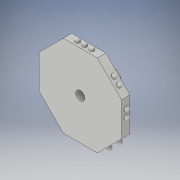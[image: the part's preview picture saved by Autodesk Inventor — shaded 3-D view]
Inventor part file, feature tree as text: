
AUTODESK INVENTOR PART (.ipt)
format: ipt  version: 2017 (Build 210142000, 142)  size: 347,648 bytes
history: native  units: in
note: dims shown in document units (in); Inventor stores cm internally (conversion verified against a paired STEP export)
features: sketch x11, extrude x10, fillet x7, pattern_circular x1
ambient origin geometry x8: Origin, YZ Plane, XZ Plane, XY Plane, X Axis, Y Axis, Z Axis, Center Point
bodies: Solid1 (feature_tree)
feature tree (29):
  extrude  "Extrusion1"  Depth=0.1181in TaperAngle=0.0deg
  extrude  "Extrusion2"  Depth=0.063in
  fillet  "Fillet1"  Radius=0.1in
  sketch  "Sketch3"  dims[d8=0.063in d9=0.063in d10=0.059in]
  sketch  "Sketch4"  dims[d11=0.0472in d12=0.0in d13=0.0315in d24=0.059in]
  sketch  "Sketch5"  dims[d25=0.063in d26=0.1in d27=0.1in d28=0.063in d29=0.063in d31=0.0575in d32=0.059in d34=0.0in d35=0.059in]
  sketch  "Sketch6"  dims[d36=0.059in]
  sketch  "Sketch7"  dims[d40=0.063in d41=0.1in d42=0.1in d43=0.063in d44=0.063in d46=0.059in d47=0.0in d48=0.059in d49=0.059in d50=0.0in d51=0.0in]
  sketch  "Sketch8"  dims[d70=0.063in d71=0.1in d72=0.1in d73=0.063in d74=0.063in d76=0.059in d77=0.0in d78=0.059in d79=0.059in d81=0.0in d82=0.0in]
  sketch  "Sketch9"  dims[d83=0.063in d84=0.1in d85=0.1in d86=0.063in d87=0.063in d89=0.059in d90=0.059in d91=0.059in d92=0.0in d93=0.0in d94=0.0in d95=0.0in]
  extrude  "Extrusion6"  Depth=0.063in
  fillet  "Fillet5"  Radius=0.059in
  extrude  "Extrusion7"  Depth=0.0315in
  fillet  "Fillet6"  Radius=0.059in
  extrude  "Extrusion8"  TaperAngle=0.0deg  [1 undecoded]
  fillet  "Fillet7"  Radius=0.059in
  extrude  "Extrusion9"  TaperAngle=0.0deg  [1 undecoded]
  fillet  "Fillet8"  [1 undecoded]
  extrude  "Extrusion10"  TaperAngle=0.0deg  [1 undecoded]
  fillet  "Fillet9"  [1 undecoded]
  extrude  "Extrusion11"  TaperAngle=0.0deg  [1 undecoded]
  fillet  "Fillet10"  [1 undecoded]
  extrude  "Extrusion14"  Depth=0.0315in
  pattern_circular  "Circular Pattern4"  [2 undecoded]
  extrude  "Extrusion15"  Depth=0.0315in
  sketch  "Sketch1"  dims[d2=0.4724in d3=0.1181in d4=0.0in]
  sketch  "Sketch2"  dims[d5=0.063in d6=0.1in d7=0.1in]
  sketch  "Sketch11"  dims[d96=0.063in d97=0.1in d98=0.1in d99=0.063in d100=0.063in d102=0.059in d103=0.059in d104=0.059in d105=0.0in d106=0.0in d107=0.0in d108=0.0in]
  sketch  "Sketch12"  dims[d109=0.063in d110=0.1in d111=0.1in d112=0.063in d113=0.063in d115=0.059in d116=0.059in d117=0.059in d118=0.0in d119=0.0in d120=0.0in d121=0.0in d122=0.0472in d123=0.0in d124=0.0315in d125=0.0472in d126=0.0in d127=0.0315in d128=0.0472in d129=0.0in d130=0.0315in d131=0.0472in d132=0.0in d133=0.0315in d134=0.0472in d135=0.0in d136=0.0315in d137=0.0472in d138=0.0in d139=0.0315in d148=0.6in d154=12.5984in d156=360.0deg d161=0.04in d162=0.04in d163=0.2681in d164=0.0in d165=3.1496in d166=360.0deg d168=0.075in d169=0.236in d170=0.236in d171=0.236in d172=0.236in d173=0.236in d175=0.236in d176=0.236in d177=0.126in d178=1.0in d179=0.0in]
note: 9 required parameter values undecoded (feature->parameter linkage not recoverable at this tier; creation-order binding heuristic only, values carry confidence <= 0.55)
